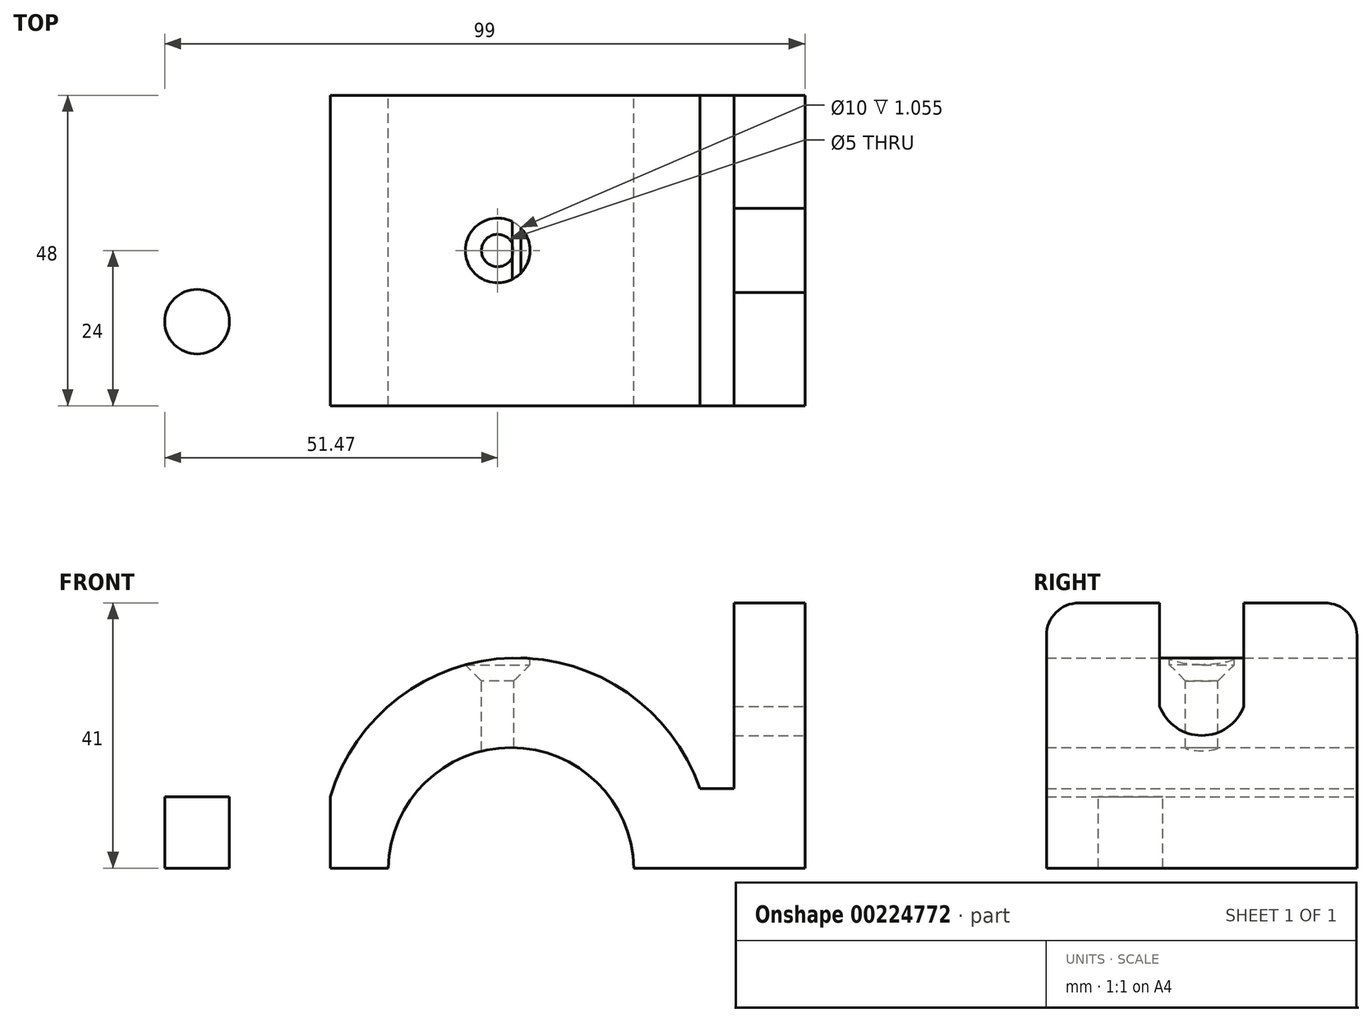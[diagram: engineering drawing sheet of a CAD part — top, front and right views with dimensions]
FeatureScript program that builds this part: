
annotation { "Feature Type Name" : "Feature", "Feature Type Description" : "" }
export const myFeature = defineFeature(function(context is Context, id is Id, definition is map)
    precondition{}
    {
        {
            var Q0;
            Q0=qCreatedBy(makeId("Front.planeOp"),FACE);
            var sketch = newSketch(context, id + "F0", { "sketchPlane" : qUnion([Q0])});
            skArc(sketch, "E0", {"start": v(21.07, 0) * mm, "mid": v(2.08, 18.64) * mm, "end": v(-16.92, 0) * mm});
            skArc(sketch, "E1", {"start": v(31.27, 12.29) * mm, "mid": v(2.24, 32.5) * mm, "end": v(-25.86, 11) * mm});
            skLineSegment(sketch, "E2", {"start": v(-25.86, 11) * mm, "end": v(-59.47, 11) * mm});
            skLineSegment(sketch, "E3", {"start": v(-59.47, 11) * mm, "end": v(-59.47, 0) * mm});
            skLineSegment(sketch, "E4", {"start": v(-59.47, 0) * mm, "end": v(-16.92, 0) * mm});
            skLineSegment(sketch, "E5", {"start": v(31.27, 12.29) * mm, "end": v(36.53, 12.29) * mm});
            skLineSegment(sketch, "E6", {"start": v(36.53, 12.29) * mm, "end": v(36.53, 41) * mm});
            skLineSegment(sketch, "E7", {"start": v(36.53, 41) * mm, "end": v(47.53, 41) * mm});
            skLineSegment(sketch, "E8", {"start": v(47.53, 41) * mm, "end": v(47.53, 0) * mm});
            skLineSegment(sketch, "E9", {"start": v(47.53, 0) * mm, "end": v(21.07, 0) * mm});
            skSolve(sketch);
        }
        {
            var Q0;
            Q0 = qSketchRegion(id + "F0", true);
            extrude(context, id + "F1", {"entities" : qUnion([Q0]), "depth" : 48 * mm, "symmetric" : true});
        }
        {
            var Q0;
            Q0=makeQuery(id+"F1.opExtrude","CAP_EDGE",EDGE,{"disambiguationData":[OSD([sQuery(id+"F0.wireOp",EDGE,"E3")])],"isStart":true});
            var Q1;
            Q1=makeQuery(id+"F1.opExtrude","CAP_EDGE",EDGE,{"disambiguationData":[OSD([sQuery(id+"F0.wireOp",EDGE,"E3")])],"isStart":false});
            fillet(context, id + "F2", {"entities" : qUnion([Q0, Q1]), "radius" : 13 * mm, "tangentPropagation" : true, "allowEdgeOverflow" : false});
        }
        {
            var Q0;
            Q0=makeQuery(id+"F1.opExtrude","SWEPT_FACE",FACE,{"disambiguationData":[OSD([sQuery(id+"F0.wireOp",EDGE,"E2")])]});
            var sketch = newSketch(context, id + "F3", { "sketchPlane" : qUnion([Q0])});
            skPoint(sketch, "E10.centerSnap0", {"position": v(-46.47, 24) * mm});
            skArc(sketch, "E11.0", {"start": v(-46.47, 24) * mm, "mid": v(-55.66, 20.2) * mm, "end": v(-59.47, 11) * mm, "construction": true});
            skArc(sketch, "E12.1", {"start": v(-59.47, -11) * mm, "mid": v(-55.66, -20.2) * mm, "end": v(-46.47, -24) * mm, "construction": true});
            skCircle(sketch, "E13", {"center": v(-46.47, 11) * mm, "radius": 5 * mm});
            skLineSegment(sketch, "E14", {"start": v(-46.47, 24) * mm, "end": v(-46.47, -24) * mm, "construction": true});
            skCircle(sketch, "E15.MirrorC", {"center": v(-46.47, -11) * mm, "radius": 5 * mm});
            skSolve(sketch);
        }
        {
            var Q0;
            Q0=makeQuery(id+"F3.imprint","IMPRINT",FACE,{"disambiguationData":[TD([[makeQuery(id+"F3.imprint","IMPRINT",EDGE,{"derivedFrom":sQuery(id+"F3.wireOp",EDGE,"E15.MirrorC")}),-1.0]])]});
            var Q1;
            Q1=makeQuery(id+"F3.imprint","IMPRINT",FACE,{"disambiguationData":[TD([[makeQuery(id+"F3.imprint","IMPRINT",EDGE,{"derivedFrom":sQuery(id+"F3.wireOp",EDGE,"E13")}),1.0]])]});
            extrude(context, id + "F4", {"entities" : qUnion([Q0, Q1]), "operationType" : NewBodyOperationType.REMOVE, "oppositeDirection" : true, "depth" : 25 * mm});
        }
        {
            var Q0;
            Q0=makeQuery(id+"F1.opExtrude","CAP_EDGE",EDGE,{"disambiguationData":[OSD([sQuery(id+"F0.wireOp",EDGE,"E7")])],"isStart":false});
            var Q1;
            Q1=makeQuery(id+"F1.opExtrude","CAP_EDGE",EDGE,{"disambiguationData":[OSD([sQuery(id+"F0.wireOp",EDGE,"E7")])],"isStart":true});
            fillet(context, id + "F5", {"entities" : qUnion([Q0, Q1]), "radius" : 5 * mm, "tangentPropagation" : true, "allowEdgeOverflow" : false});
        }
        {
            var Q0;
            Q0=makeQuery(id+"F1.opExtrude","SWEPT_FACE",FACE,{"disambiguationData":[OSD([sQuery(id+"F0.wireOp",EDGE,"E8")])]});
            var sketch = newSketch(context, id + "F6", { "sketchPlane" : qUnion([Q0])});
            skLineSegment(sketch, "E16", {"start": v(0, 41) * mm, "end": v(0, 0) * mm, "construction": true});
            skLineSegment(sketch, "E17", {"start": v(-24, 25) * mm, "end": v(24, 25) * mm, "construction": true});
            skPoint(sketch, "E17.startSnap0", {"position": v(0, 20.5) * mm});
            skArc(sketch, "E18", {"start": v(-6.5, 25) * mm, "mid": v(0, 20.5) * mm, "end": v(6.5, 25) * mm});
            skLineSegment(sketch, "E19", {"start": v(-6.5, 25) * mm, "end": v(-6.5, 41) * mm});
            skLineSegment(sketch, "E20", {"start": v(6.5, 25) * mm, "end": v(6.5, 41) * mm});
            skSolve(sketch);
        }
        {
            var Q0;
            Q0=makeQuery(id+"F6.imprint","IMPRINT",FACE,{"disambiguationData":[TD([[makeQuery(id+"F6.imprint","IMPRINT",EDGE,{"derivedFrom":sQuery(id+"F6.wireOp",EDGE,"E18")}),1.0]])]});
            extrude(context, id + "F7", {"entities" : qUnion([Q0]), "operationType" : NewBodyOperationType.REMOVE, "oppositeDirection" : true, "depth" : 12.6 * mm});
        }
        {
            var Q0;
            Q0=makeQuery(id+"F1.opExtrude","CAP_EDGE",EDGE,{"disambiguationData":[OSD([sQuery(id+"F0.wireOp",EDGE,"E1")])],"isStart":false});
            cPoint(context, id + "F8", {"entities" : qUnion([Q0]), "parameter" : 0.5});
        }
        {
            var Q0;
            Q0 = qCreatedBy(id + "F8" ,VERTEX);
            var Q1;
            Q1=qCreatedBy(makeId("Top.planeOp"),FACE);
            cPlane(context, id + "F9", {"entities" : qUnion([Q0, Q1]), "cplaneType" : CPlaneType.PLANE_POINT, "offset" : 25.4 * mm, "width" : 152.4 * mm, "height" : 152.4 * mm});
        }
        {
            var Q0;
            Q0=qCreatedBy(id+"F9.planeOp",FACE);
            var sketch = newSketch(context, id + "F10", { "sketchPlane" : qUnion([Q0])});
            skPoint(sketch, "E21", {"position": v(0, 0) * mm});
            skSolve(sketch);
        }
        {
            var Q0;
            Q0=sQuery(id+"F10.wireOp",VERTEX,"E21");
            var Q1;
            Q1=makeQuery(id+"F1.opExtrude","SWEPT_BODY",BODY,{"disambiguationData":[OSD([sQuery(id+"F0.wireOp",EDGE,"E0"),sQuery(id+"F0.wireOp",EDGE,"E1"),sQuery(id+"F0.wireOp",EDGE,"E2"),sQuery(id+"F0.wireOp",EDGE,"E3"),sQuery(id+"F0.wireOp",EDGE,"E4"),sQuery(id+"F0.wireOp",EDGE,"E5"),sQuery(id+"F0.wireOp",EDGE,"E6"),sQuery(id+"F0.wireOp",EDGE,"E7"),sQuery(id+"F0.wireOp",EDGE,"E8"),sQuery(id+"F0.wireOp",EDGE,"E9")])]});
            hole(context, id + "F11", {"style" : HoleStyle.C_SINK, "endStyle" : HoleEndStyle.THROUGH, "holeDiameter" : 5 * mm, "cSinkDiameter" : 10 * mm, "cSinkAngle" : 90 * degree, "locations" : qUnion([Q0]), "scope" : qUnion([Q1]), "isTappedThrough" : true});
        }
    });
